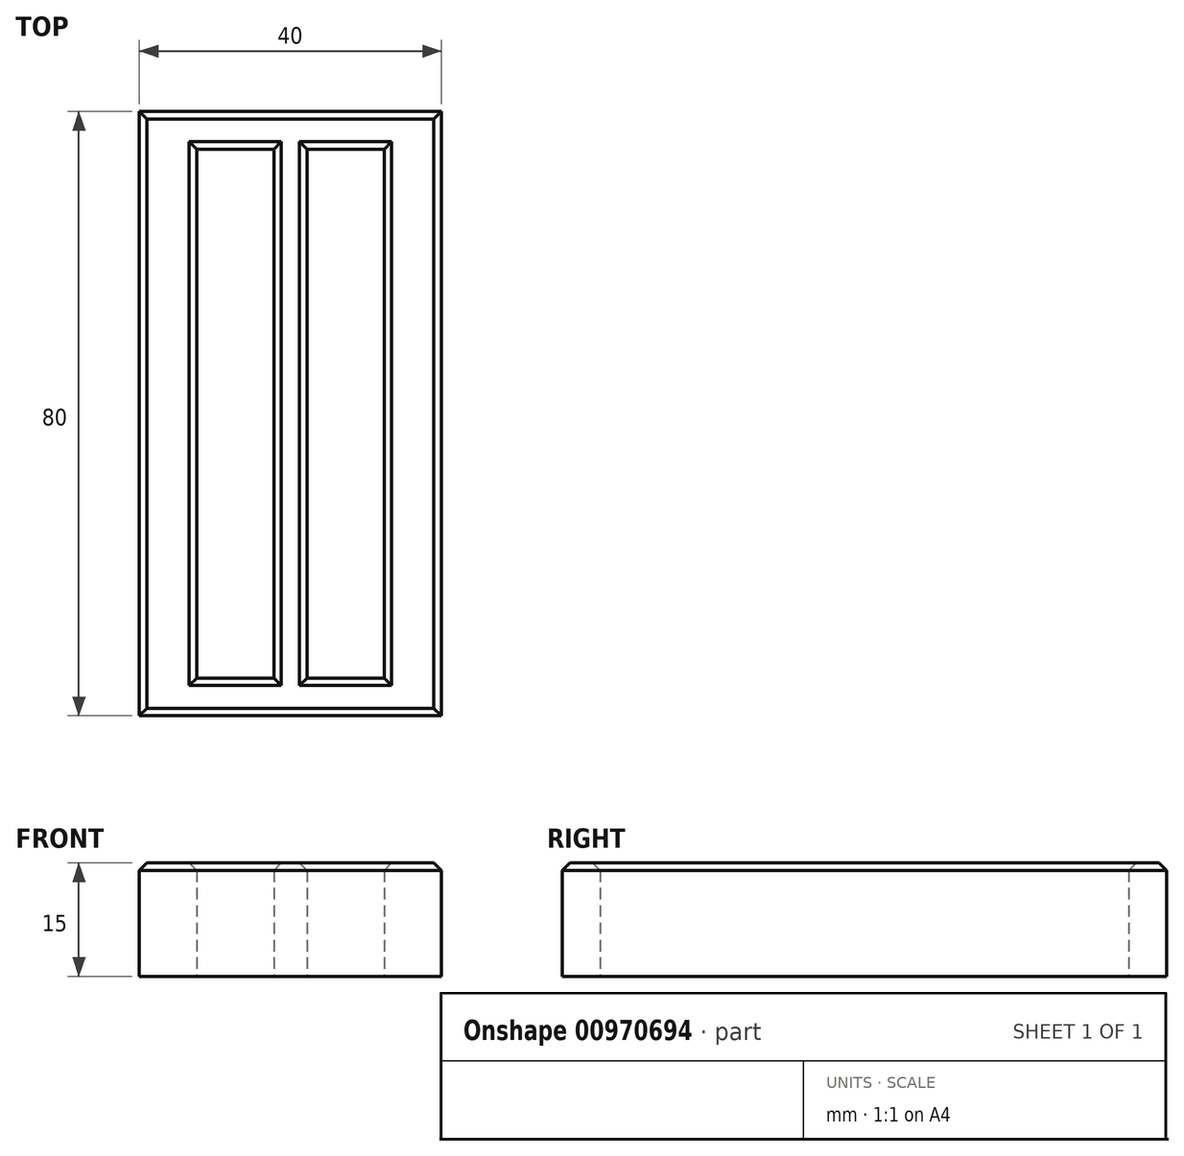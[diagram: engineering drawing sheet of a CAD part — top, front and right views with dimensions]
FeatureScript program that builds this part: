
annotation { "Feature Type Name" : "Feature", "Feature Type Description" : "" }
export const myFeature = defineFeature(function(context is Context, id is Id, definition is map)
    precondition{}
    {
        {
            var Q0;
            Q0=qCreatedBy(makeId("Top.planeOp"),FACE);
            var sketch = newSketch(context, id + "F0", { "sketchPlane" : qUnion([Q0])});
            skLineSegment(sketch, "E0", {"start": v(0, 0) * mm, "end": v(-20, 0) * mm});
            skLineSegment(sketch, "E1", {"start": v(-20, 0) * mm, "end": v(-20, -80) * mm});
            skLineSegment(sketch, "E2", {"start": v(-20, -80) * mm, "end": v(0, -80) * mm});
            skLineSegment(sketch, "E3", {"start": v(0, 0) * mm, "end": v(0, -80) * mm, "construction": true});
            skLineSegment(sketch, "E4.bottom", {"start": v(-12.4, -5) * mm, "end": v(-2.2, -5) * mm});
            skLineSegment(sketch, "E4.top", {"start": v(-12.4, -75) * mm, "end": v(-2.2, -75) * mm});
            skLineSegment(sketch, "E4.left", {"start": v(-12.4, -5) * mm, "end": v(-12.4, -75) * mm});
            skLineSegment(sketch, "E4.right", {"start": v(-2.2, -5) * mm, "end": v(-2.2, -75) * mm});
            skLineSegment(sketch, "E5.MirrorCS", {"start": v(20, -80) * mm, "end": v(0, -80) * mm});
            skLineSegment(sketch, "E6.MirrorCS", {"start": v(12.4, -5) * mm, "end": v(2.2, -5) * mm});
            skLineSegment(sketch, "E7.MirrorCS", {"start": v(0, 0) * mm, "end": v(20, 0) * mm});
            skLineSegment(sketch, "E8.MirrorCS", {"start": v(2.2, -5) * mm, "end": v(2.2, -75) * mm});
            skLineSegment(sketch, "E9.MirrorCS", {"start": v(20, 0) * mm, "end": v(20, -80) * mm});
            skLineSegment(sketch, "E10.MirrorCS", {"start": v(12.4, -75) * mm, "end": v(2.2, -75) * mm});
            skLineSegment(sketch, "E11.MirrorCS", {"start": v(12.4, -5) * mm, "end": v(12.4, -75) * mm});
            skSolve(sketch);
        }
        {
            var Q0;
            Q0=makeQuery(id+"F0.imprint","IMPRINT",FACE,{"disambiguationData":[TD([[makeQuery(id+"F0.imprint","IMPRINT",EDGE,{"derivedFrom":sQuery(id+"F0.wireOp",EDGE,"E0")}),1.0]])]});
            extrude(context, id + "F1", {"entities" : qUnion([Q0]), "depth" : 15 * mm, "offsetDistance" : 25 * mm});
        }
        {
            var Q0;
            Q0=makeQuery(id+"F1.opExtrude","CAP_FACE",FACE,{"disambiguationData":[OSD([sQuery(id+"F0.wireOp",EDGE,"E0"),sQuery(id+"F0.wireOp",EDGE,"E1"),sQuery(id+"F0.wireOp",EDGE,"E2"),sQuery(id+"F0.wireOp",EDGE,"E4.bottom"),sQuery(id+"F0.wireOp",EDGE,"E4.top"),sQuery(id+"F0.wireOp",EDGE,"E4.left"),sQuery(id+"F0.wireOp",EDGE,"E4.right"),sQuery(id+"F0.wireOp",EDGE,"E5.MirrorCS"),sQuery(id+"F0.wireOp",EDGE,"E6.MirrorCS"),sQuery(id+"F0.wireOp",EDGE,"E7.MirrorCS"),sQuery(id+"F0.wireOp",EDGE,"E8.MirrorCS"),sQuery(id+"F0.wireOp",EDGE,"E9.MirrorCS"),sQuery(id+"F0.wireOp",EDGE,"E10.MirrorCS"),sQuery(id+"F0.wireOp",EDGE,"E11.MirrorCS")])],"isStart":false});
            chamfer(context, id + "F2", {"entities" : qUnion([Q0]), "width" : 1 * mm, "tangentPropagation" : true});
        }
    });
